# Revit family: 303_R403X_-right+R460
name_source: partatom
category: Pipe Accessories
revit_build: Autodesk Revit 2018 (Build: 20170223_1515(x64)
units: mm (PartAtom-declared; Revit-internal decimal feet)

## family parameters
Always vertical = Yes
Cut with Voids When Loaded = No
Part Type = Valve - Breaks Into
Round Connector Dimension = Use Diameter
Shared = No
Work Plane-Based = No

## types (3) — shared parameters
CAT0 = Yes
CenSd_W2_6 = 13 mm
Description = Valve with thermostatic option with protection cover, angle version. Available in 1/2” size, right
L2D = 38 mm  [stored 0.124672 ft]
L2D_Min = 3048 mm  [stored 10 ft]
M1 = 12 mm  [stored 0.0393701 ft]
M3 = 14 mm  [stored 0.0459318 ft]
M3__ve = -14 mm
Manufacturer = Giacomini
QmdConnectorList = 301;D;302;D1
S1 = 12 mm  [stored 0.0393701 ft]
S1__ve = -12 mm  [stored -0.0393701 ft]
T4 = 11 mm
T4__ve = -11 mm
TR = 100 mm  [stored 0.328084 ft]
TR1 = 20 mm  [stored 0.0656168 ft]
TR__ve = -100 mm  [stored -0.328084 ft]
URL = http://www.giacomini.com
W1 = 12 mm  [stored 0.0393701 ft]
W2 = 15 mm  [stored 0.0492126 ft]
magiPartTypeId = 303
magiProductFamilyId = R403X*-right+R460
zero-valued in all types: MC_Default_elevation

## per-type parameters (varying)
| type | B1 | D | D1 | G3 | HT1 | L | L2 | L3 | L3__ve | L4 | L4__ve | L5 | L5__ve | R1 | T1 | T2 | T2__ve | T3 | W2D | X4 |
| R403X034-right+R460 | 5 mm  [stored 0.0164042 ft] | 18 mm | 15 mm | 9 mm  [stored 0.0295276 ft] | 19 mm  [stored 0.062336 ft] | 38 mm  [stored 0.124672 ft] | 51 mm | 8 mm  [stored 0.0262467 ft] | -8 mm | 8 mm  [stored 0.0262467 ft] | -8 mm | 4 mm  [stored 0.0131234 ft] | -4 mm | 8 mm  [stored 0.0262467 ft] | 7 mm  [stored 0.0229659 ft] | 16 mm | -16 mm | 8 mm  [stored 0.0262467 ft] | 18 mm  [stored 0.0590551 ft] | 5 mm  [stored 0.0164042 ft] |
| R403X064-right+R460 | 4 mm  [stored 0.0131234 ft] | 15 mm | 15 mm | 9 mm  [stored 0.0295276 ft] | 20 mm  [stored 0.0656168 ft] | 43 mm | 57 mm | 10 mm  [stored 0.0328084 ft] | -10 mm  [stored -0.0328084 ft] | 10 mm  [stored 0.0328084 ft] | -10 mm  [stored -0.0328084 ft] | 5 mm  [stored 0.0164042 ft] | -5 mm | 8 mm  [stored 0.0262467 ft] | 6 mm  [stored 0.019685 ft] | 15 mm  [stored 0.0492126 ft] | -15 mm | 7 mm  [stored 0.0229659 ft] | 15 mm  [stored 0.0492126 ft] | 6 mm  [stored 0.019685 ft] |
| R403X062-right+R460 | 3 mm  [stored 0.00984252 ft] | 10 mm | 10 mm | 7 mm  [stored 0.0229659 ft] | 20 mm  [stored 0.0656168 ft] | 43 mm | 57 mm | 10 mm  [stored 0.0328084 ft] | -10 mm  [stored -0.0328084 ft] | 10 mm  [stored 0.0328084 ft] | -10 mm  [stored -0.0328084 ft] | 5 mm  [stored 0.0164042 ft] | -5 mm | 5 mm  [stored 0.0164042 ft] | 4 mm  [stored 0.0131234 ft] | 13 mm | -13 mm | 5 mm  [stored 0.0164042 ft] | 10 mm  [stored 0.0328084 ft] | 6 mm  [stored 0.019685 ft] |

note: column(s) folded — value = type name in every type: magiProductCode, magiProductId

note: [stored X ft] marks values corroborated as IEEE doubles in the binary element streams (Revit-internal decimal feet)

## geometry (parser evidence)
native form markers: Sweep x2
no freeform markers — native parametric forms only
